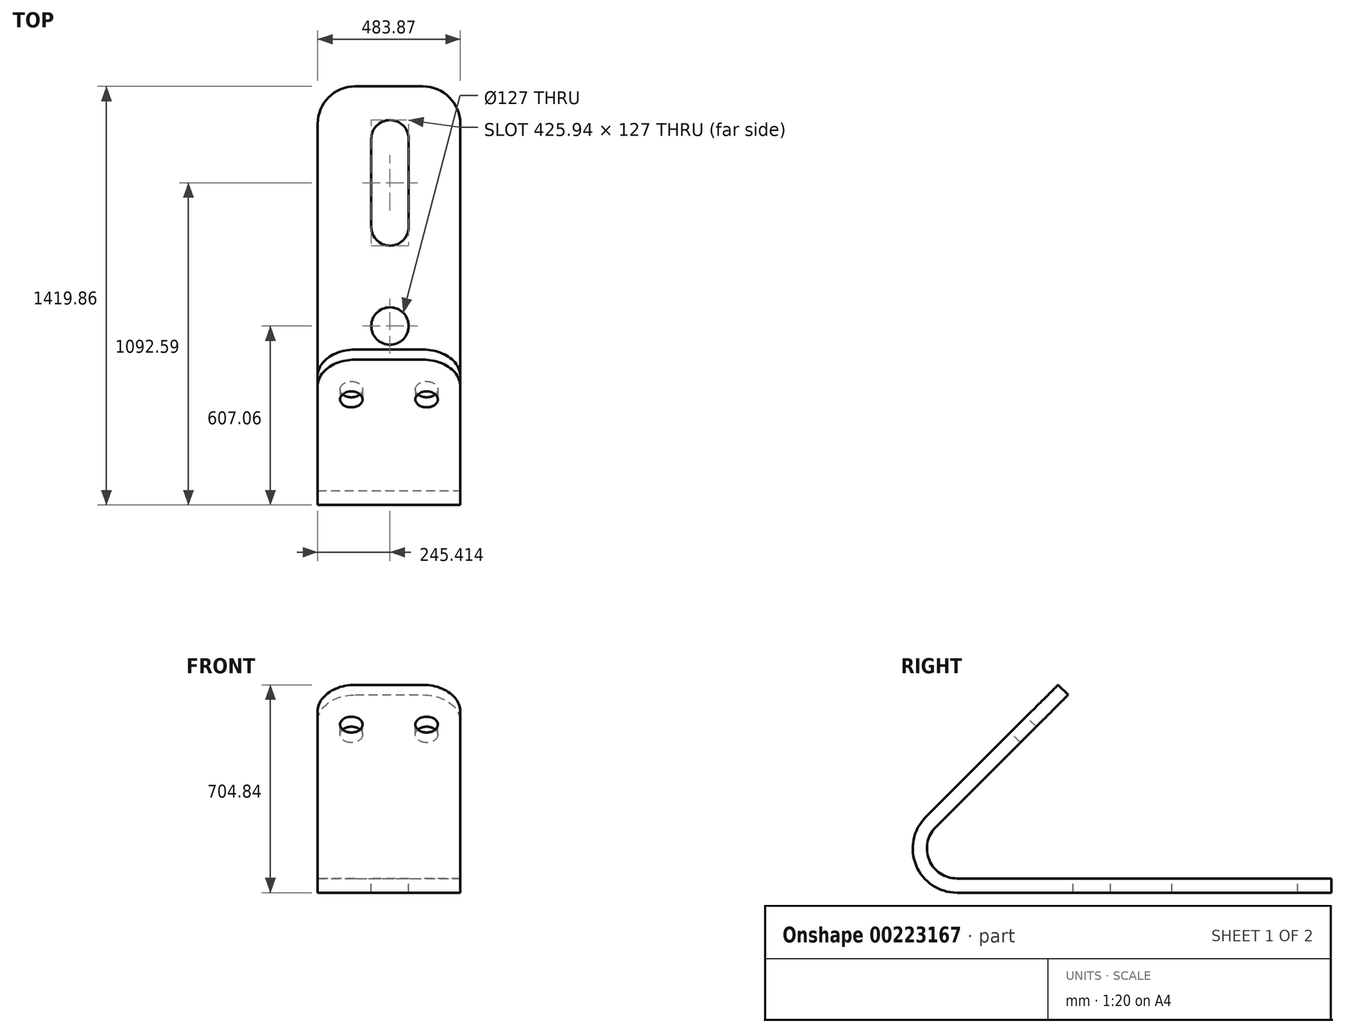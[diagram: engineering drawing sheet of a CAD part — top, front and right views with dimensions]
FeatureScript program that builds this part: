
annotation { "Feature Type Name" : "Feature", "Feature Type Description" : "" }
export const myFeature = defineFeature(function(context is Context, id is Id, definition is map)
    precondition{}
    {
        {
            var Q0;
            Q0=qCreatedBy(makeId("Right.planeOp"),FACE);
            var sketch = newSketch(context, id + "F0", { "sketchPlane" : qUnion([Q0])});
            skLineSegment(sketch, "E0", {"start": v(-635, 0) * mm, "end": v(635, 0) * mm});
            skLineSegment(sketch, "E1", {"start": v(-706.84, 173.44) * mm, "end": v(-257.83, 622.45) * mm});
            skArc(sketch, "E2", {"start": v(-706.84, 173.44) * mm, "mid": v(-728.87, 62.72) * mm, "end": v(-635, 0) * mm});
            skLineSegment(sketch, "E3.0", {"start": v(-635, -48.26) * mm, "end": v(635, -48.26) * mm});
            skArc(sketch, "E3.1", {"start": v(-740.97, 207.57) * mm, "mid": v(-773.45, 44.25) * mm, "end": v(-635, -48.26) * mm});
            skLineSegment(sketch, "E3.2", {"start": v(-740.97, 207.57) * mm, "end": v(-291.95, 656.58) * mm});
            skLineSegment(sketch, "E4", {"start": v(635, 0) * mm, "end": v(635, -48.26) * mm});
            skLineSegment(sketch, "E5", {"start": v(-291.95, 656.58) * mm, "end": v(-257.83, 622.45) * mm});
            skSolve(sketch);
        }
        {
            var Q0;
            Q0 = qSketchRegion(id + "F0", true);
            extrude(context, id + "F1", {"entities" : qUnion([Q0]), "oppositeDirection" : true, "depth" : 483.87 * mm});
        }
        {
            var Q0;
            Q0=makeQuery(id+"F1.opExtrude","SWEPT_FACE",FACE,{"disambiguationData":[OSD([sQuery(id+"F0.wireOp",EDGE,"E0")])]});
            var sketch = newSketch(context, id + "F2", { "sketchPlane" : qUnion([Q0])});
            skCircle(sketch, "E6", {"center": v(-238.46, -177.8) * mm, "radius": 63.5 * mm});
            skLineSegment(sketch, "E7", {"start": v(-238.46, -177.8) * mm, "end": v(-238.46, 457.2) * mm, "construction": true});
            skArc(sketch, "E8", {"start": v(-174.96, 457.2) * mm, "mid": v(-238.46, 520.7) * mm, "end": v(-301.96, 457.2) * mm});
            skArc(sketch, "E9", {"start": v(-301.96, 158.26) * mm, "mid": v(-238.46, 94.76) * mm, "end": v(-174.96, 158.26) * mm});
            skLineSegment(sketch, "E10", {"start": v(-301.96, 158.26) * mm, "end": v(-301.96, 457.2) * mm});
            skLineSegment(sketch, "E11", {"start": v(-174.96, 158.26) * mm, "end": v(-174.96, 457.2) * mm});
            skPoint(sketch, "E12.end.orphan", {"position": v(-238.46, 520.7) * mm});
            skSolve(sketch);
        }
        {
            var Q0;
            Q0 = qSketchRegion(id + "F2", true);
            extrude(context, id + "F3", {"entities" : qUnion([Q0]), "operationType" : NewBodyOperationType.REMOVE, "endBound" : BoundingType.THROUGH_ALL, "oppositeDirection" : true, "depth" : 25.4 * mm});
        }
        {
            var Q0;
            Q0=makeQuery(id+"F1.opExtrude","SWEPT_FACE",FACE,{"disambiguationData":[OSD([sQuery(id+"F0.wireOp",EDGE,"E3.2")])]});
            var sketch = newSketch(context, id + "F4", { "sketchPlane" : qUnion([Q0])});
            skCircle(sketch, "E13", {"center": v(-369.57, 67.33) * mm, "radius": 38.1 * mm});
            skCircle(sketch, "E14", {"center": v(-114.3, 67.33) * mm, "radius": 38.1 * mm});
            skSolve(sketch);
        }
        {
            var Q0;
            Q0 = qSketchRegion(id + "F4", true);
            var Q1;
            Q1=makeQuery(id+"F1.opExtrude","SWEPT_FACE",FACE,{"disambiguationData":[OSD([sQuery(id+"F0.wireOp",EDGE,"E1")])]});
            extrude(context, id + "F5", {"entities" : qUnion([Q0]), "operationType" : NewBodyOperationType.REMOVE, "endBound" : BoundingType.UP_TO_SURFACE, "oppositeDirection" : true, "endBoundEntityFace" : qUnion([Q1]), "depth" : 76.2 * mm});
        }
        {
            var Q0;
            Q0=makeQuery(id+"F1.opExtrude","SWEPT_FACE",FACE,{"disambiguationData":[OSD([sQuery(id+"F0.wireOp",EDGE,"E0")])]});
            var sketch = newSketch(context, id + "F6", { "sketchPlane" : qUnion([Q0])});
            skLineSegment(sketch, "E15.0", {"start": v(0, -635) * mm, "end": v(0, 508) * mm});
            skLineSegment(sketch, "E16.0", {"start": v(-356.87, 635) * mm, "end": v(-127, 635) * mm});
            skLineSegment(sketch, "E17.0", {"start": v(-483.87, -635) * mm, "end": v(-483.87, 508) * mm});
            skPoint(sketch, "E18.visualSharp", {"position": v(0, 635) * mm});
            skArc(sketch, "E18.filletArc", {"start": v(0, 508) * mm, "mid": v(-37.2, 597.8) * mm, "end": v(-127, 635) * mm});
            skPoint(sketch, "E19.visualSharp", {"position": v(-483.87, 635) * mm});
            skArc(sketch, "E19.filletArc", {"start": v(-356.87, 635) * mm, "mid": v(-446.67, 597.8) * mm, "end": v(-483.87, 508) * mm});
            skSolve(sketch);
        }
        {
            var Q0;
            {var subQ0=sQuery(id+"F6.wireOp",EDGE,"E18.filletArc");Q0=makeQuery(id+"F6.imprint","IMPRINT",FACE,{"disambiguationData":[TD([[makeQuery(id+"F6.imprint","IMPRINT",EDGE,{"derivedFrom":subQ0}),-1.0]])]});}
            var Q1;
            {var subQ0=sQuery(id+"F6.wireOp",EDGE,"E19.filletArc");Q1=makeQuery(id+"F6.imprint","IMPRINT",FACE,{"disambiguationData":[TD([[makeQuery(id+"F6.imprint","IMPRINT",EDGE,{"derivedFrom":subQ0}),-1.0]])]});}
            extrude(context, id + "F7", {"entities" : qUnion([Q0, Q1]), "operationType" : NewBodyOperationType.REMOVE, "endBound" : BoundingType.THROUGH_ALL, "oppositeDirection" : true, "depth" : 25.4 * mm});
        }
        {
            var Q0;
            Q0=makeQuery(id+"F1.opExtrude","SWEPT_FACE",FACE,{"disambiguationData":[OSD([sQuery(id+"F0.wireOp",EDGE,"E3.2")])]});
            var sketch = newSketch(context, id + "F8", { "sketchPlane" : qUnion([Q0])});
            skLineSegment(sketch, "E20.0", {"start": v(-356.87, 257.83) * mm, "end": v(-127, 257.83) * mm});
            skLineSegment(sketch, "E21.0", {"start": v(-483.87, -377.17) * mm, "end": v(-483.87, 130.83) * mm});
            skLineSegment(sketch, "E22.0", {"start": v(0, -377.17) * mm, "end": v(0, 130.83) * mm});
            skPoint(sketch, "E23.visualSharp", {"position": v(-483.87, 257.83) * mm});
            skArc(sketch, "E23.filletArc", {"start": v(-356.87, 257.83) * mm, "mid": v(-446.67, 220.63) * mm, "end": v(-483.87, 130.83) * mm});
            skPoint(sketch, "E24.visualSharp", {"position": v(0, 257.83) * mm});
            skArc(sketch, "E24.filletArc", {"start": v(0, 130.83) * mm, "mid": v(-37.2, 220.63) * mm, "end": v(-127, 257.83) * mm});
            skSolve(sketch);
        }
        {
            var Q0;
            {var subQ0=sQuery(id+"F8.wireOp",EDGE,"E23.filletArc");Q0=makeQuery(id+"F8.imprint","IMPRINT",FACE,{"disambiguationData":[TD([[makeQuery(id+"F8.imprint","IMPRINT",EDGE,{"derivedFrom":subQ0}),-1.0]])]});}
            var Q1;
            {var subQ0=sQuery(id+"F8.wireOp",EDGE,"E24.filletArc");Q1=makeQuery(id+"F8.imprint","IMPRINT",FACE,{"disambiguationData":[TD([[makeQuery(id+"F8.imprint","IMPRINT",EDGE,{"derivedFrom":subQ0}),-1.0]])]});}
            extrude(context, id + "F9", {"entities" : qUnion([Q0, Q1]), "operationType" : NewBodyOperationType.REMOVE, "endBound" : BoundingType.UP_TO_NEXT, "oppositeDirection" : true, "depth" : 25.4 * mm});
        }
    });
